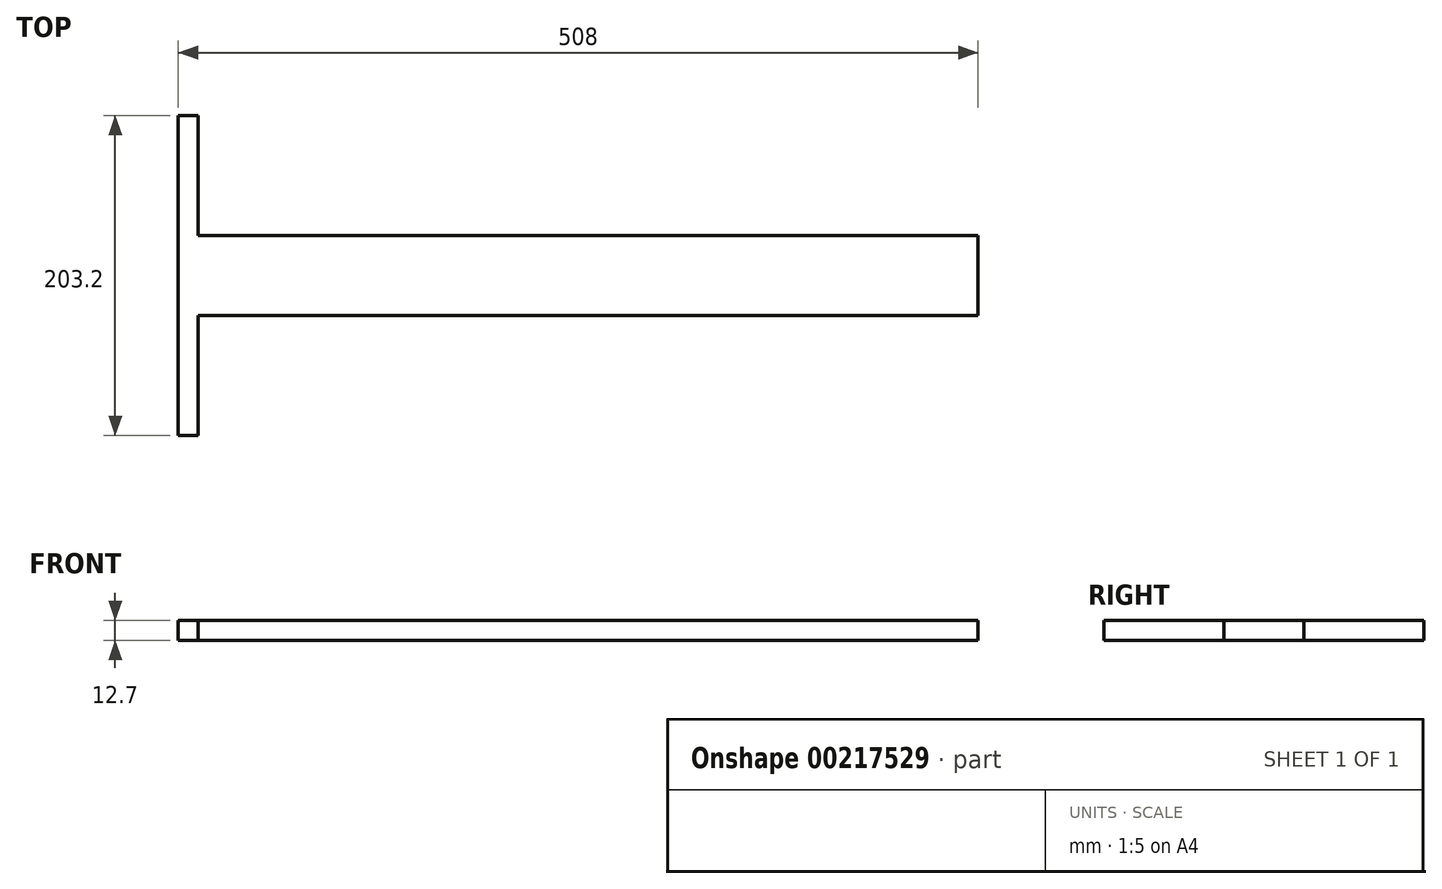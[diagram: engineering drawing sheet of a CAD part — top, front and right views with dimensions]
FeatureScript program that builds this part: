
annotation { "Feature Type Name" : "Feature", "Feature Type Description" : "" }
export const myFeature = defineFeature(function(context is Context, id is Id, definition is map)
    precondition{}
    {
        {
            var Q0;
            Q0=qCreatedBy(makeId("Top.planeOp"),FACE);
            var sketch = newSketch(context, id + "F0", { "sketchPlane" : qUnion([Q0])});
            skLineSegment(sketch, "E0.bottom", {"start": v(-12.7, 101.6) * mm, "end": v(0, 101.6) * mm});
            skLineSegment(sketch, "E0.top", {"start": v(-12.7, -101.6) * mm, "end": v(0, -101.6) * mm});
            skLineSegment(sketch, "E0.left", {"start": v(-12.7, 101.6) * mm, "end": v(-12.7, -101.6) * mm});
            skLineSegment(sketch, "E0.right", {"start": v(0, 101.6) * mm, "end": v(0, -101.6) * mm});
            skLineSegment(sketch, "E1.bottom", {"start": v(0, 25.4) * mm, "end": v(495.3, 25.4) * mm});
            skLineSegment(sketch, "E1.top", {"start": v(0, -25.4) * mm, "end": v(495.3, -25.4) * mm});
            skLineSegment(sketch, "E1.left", {"start": v(0, 25.4) * mm, "end": v(0, -25.4) * mm});
            skLineSegment(sketch, "E1.right", {"start": v(495.3, 25.4) * mm, "end": v(495.3, -25.4) * mm});
            skSolve(sketch);
        }
        {
            var Q0;
            Q0 = qSketchRegion(id + "F0", true);
            extrude(context, id + "F1", {"entities" : qUnion([Q0]), "depth" : 12.7 * mm});
        }
    });
